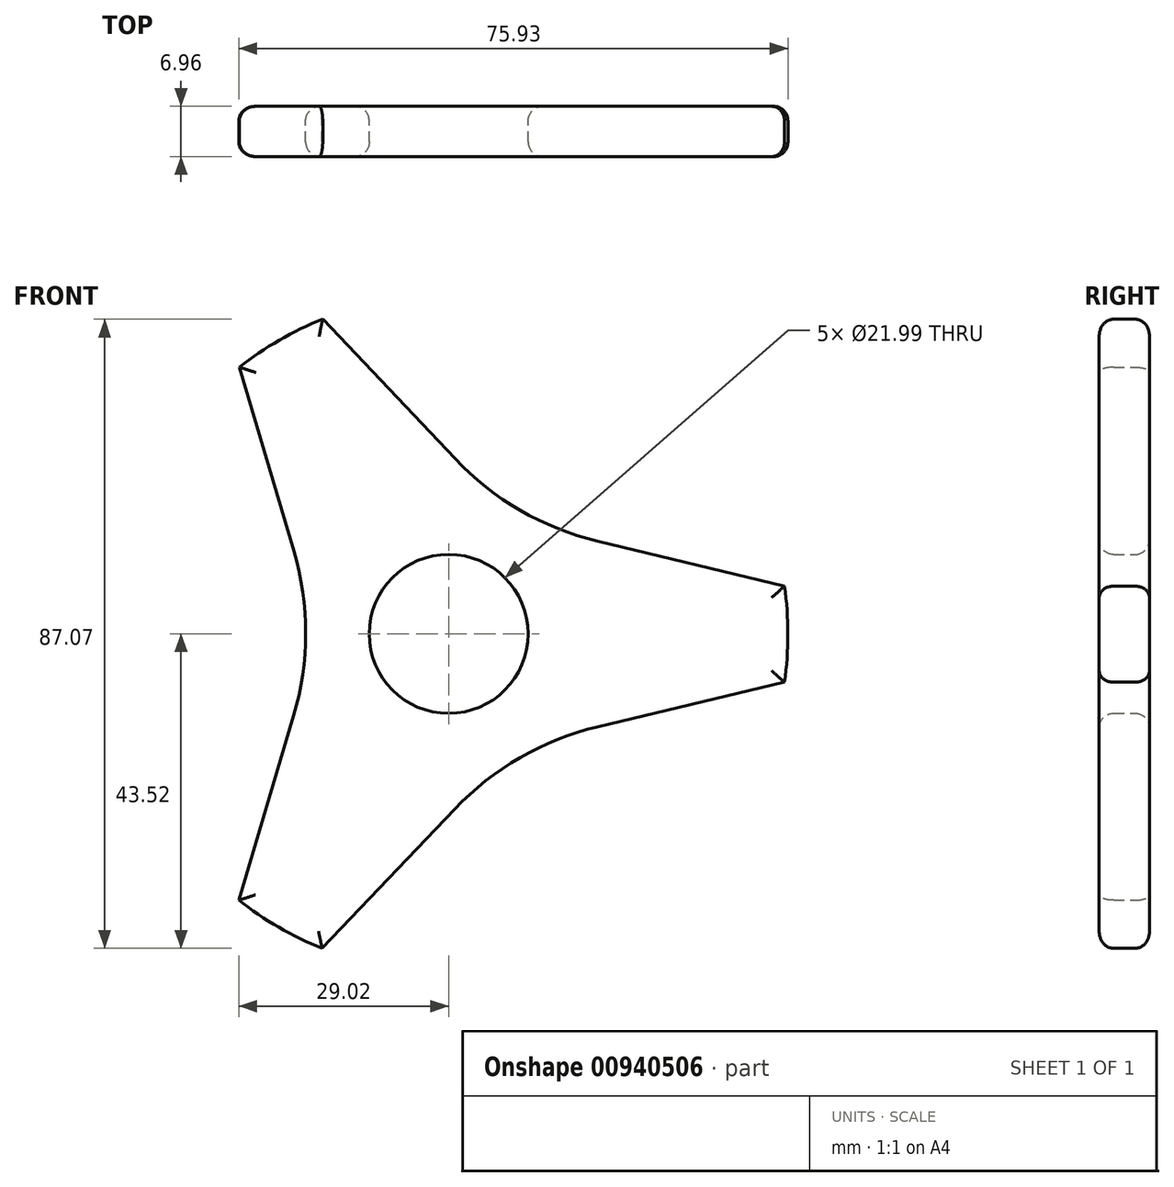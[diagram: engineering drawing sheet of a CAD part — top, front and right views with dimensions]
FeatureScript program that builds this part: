
annotation { "Feature Type Name" : "Feature", "Feature Type Description" : "" }
export const myFeature = defineFeature(function(context is Context, id is Id, definition is map)
    precondition{}
    {
        {
            var Q0;
            Q0=qCreatedBy(makeId("Front.planeOp"),FACE);
            var sketch = newSketch(context, id + "F0", { "sketchPlane" : qUnion([Q0])});
            skCircle(sketch, "E0", {"center": v(0, 0) * mm, "radius": 11 * mm});
            skCircle(sketch, "E1", {"center": v(0, 0) * mm, "radius": 17.3 * mm});
            skPoint(sketch, "E2.0.midPoint", {"position": v(55.6, -32.17) * mm});
            skLineSegment(sketch, "E3", {"start": v(23.49, 40.6) * mm, "end": v(8.66, 14.97) * mm});
            skLineSegment(sketch, "E4", {"start": v(23.42, -40.64) * mm, "end": v(8.64, -14.99) * mm});
            skLineSegment(sketch, "E5", {"start": v(9.03, 15.62) * mm, "end": v(23.49, 40.6) * mm});
            skLineSegment(sketch, "E6", {"start": v(-28.95, 36.9) * mm, "end": v(-21.41, 11.43) * mm});
            skLineSegment(sketch, "E7", {"start": v(-21.43, -11.3) * mm, "end": v(-29.02, -36.85) * mm});
            skLineSegment(sketch, "E8", {"start": v(-17.5, -43.52) * mm, "end": v(0.84, -24.23) * mm});
            skLineSegment(sketch, "E9", {"start": v(20.54, -12.88) * mm, "end": v(46.43, -6.7) * mm});
            skArc(sketch, "E10", {"start": v(46.43, -6.7) * mm, "mid": v(46.9, -0.04) * mm, "end": v(46.44, 6.61) * mm});
            skPoint(sketch, "E11.visualSharp", {"position": v(9.03, 15.62) * mm});
            skPoint(sketch, "E12.visualSharp", {"position": v(-18.05, 0.06) * mm});
            skArc(sketch, "E12.filletArc", {"start": v(-21.43, -11.3) * mm, "mid": v(-19.77, 0.06) * mm, "end": v(-21.41, 11.43) * mm});
            skArc(sketch, "E13.filletArc", {"start": v(0.88, 24.23) * mm, "mid": v(9.9, 17.1) * mm, "end": v(20.56, 12.84) * mm});
            skPoint(sketch, "E14.visualSharp", {"position": v(9, -15.63) * mm});
            skArc(sketch, "E14.filletArc", {"start": v(20.54, -12.88) * mm, "mid": v(9.87, -17.12) * mm, "end": v(0.84, -24.23) * mm});
            skLineSegment(sketch, "E15.trimOffspring", {"start": v(-17.42, 43.55) * mm, "end": v(0.88, 24.23) * mm});
            skLineSegment(sketch, "E16.trimOffspring", {"start": v(-23.42, 40.64) * mm, "end": v(-8.64, 14.99) * mm});
            skLineSegment(sketch, "E17.trimOffspring", {"start": v(-19.77, 0.02) * mm, "end": v(-17.3, 0.01) * mm});
            skPoint(sketch, "E18.start.orphan", {"position": v(-74.18, 0.06) * mm});
            skLineSegment(sketch, "E19.trimOffspring", {"start": v(-23.49, -40.6) * mm, "end": v(-8.66, -14.97) * mm});
            skPoint(sketch, "E20.orphan", {"position": v(37.03, -64.27) * mm});
            skLineSegment(sketch, "E21.trimOffspring", {"start": v(46.9, -0.04) * mm, "end": v(17.3, -0.01) * mm});
            skLineSegment(sketch, "E22", {"start": v(20.56, 12.84) * mm, "end": v(46.44, 6.61) * mm});
            skPoint(sketch, "E23.start.orphan", {"position": v(74.18, -0.06) * mm});
            skArc(sketch, "E24.trimOffspring", {"start": v(-17.42, 43.55) * mm, "mid": v(-23.42, 40.64) * mm, "end": v(-28.95, 36.9) * mm});
            skArc(sketch, "E25.trimOffspring", {"start": v(-29.02, -36.85) * mm, "mid": v(-23.5, -40.6) * mm, "end": v(-17.5, -43.52) * mm});
            skSolve(sketch);
        }
        {
            var Q0;
            Q0 = qSketchRegion(id + "F0", true);
            var Q1;
            Q1=makeQuery(id+"F0.imprint","IMPRINT",FACE,{"disambiguationData":[TD([[makeQuery(id+"F0.imprint","IMPRINT",EDGE,{"derivedFrom":sQuery(id+"F0.wireOp",EDGE,"E0")}),-1.0]])]});
            extrude(context, id + "F1", {"entities" : qUnion([Q0, Q1]), "depth" : 6.96 * mm, "offsetDistance" : 25 * mm});
        }
        {
            var Q0;
            Q0=makeQuery(id+"F1.opExtrude","CAP_FACE",FACE,{"disambiguationData":[OSD([sQuery(id+"F0.wireOp",EDGE,"E1"),sQuery(id+"F0.wireOp",EDGE,"E6"),sQuery(id+"F0.wireOp",EDGE,"E7"),sQuery(id+"F0.wireOp",EDGE,"E8"),sQuery(id+"F0.wireOp",EDGE,"E9"),sQuery(id+"F0.wireOp",EDGE,"E10"),sQuery(id+"F0.wireOp",EDGE,"E12.filletArc"),sQuery(id+"F0.wireOp",EDGE,"E13.filletArc"),sQuery(id+"F0.wireOp",EDGE,"E14.filletArc"),sQuery(id+"F0.wireOp",EDGE,"E15.trimOffspring"),sQuery(id+"F0.wireOp",EDGE,"E22"),sQuery(id+"F0.wireOp",EDGE,"E24.trimOffspring"),sQuery(id+"F0.wireOp",EDGE,"E25.trimOffspring")])],"isStart":false});
            var Q1;
            Q1=makeQuery(id+"F1.opExtrude","CAP_FACE",FACE,{"disambiguationData":[OSD([sQuery(id+"F0.wireOp",EDGE,"E1"),sQuery(id+"F0.wireOp",EDGE,"E6"),sQuery(id+"F0.wireOp",EDGE,"E7"),sQuery(id+"F0.wireOp",EDGE,"E8"),sQuery(id+"F0.wireOp",EDGE,"E9"),sQuery(id+"F0.wireOp",EDGE,"E10"),sQuery(id+"F0.wireOp",EDGE,"E12.filletArc"),sQuery(id+"F0.wireOp",EDGE,"E13.filletArc"),sQuery(id+"F0.wireOp",EDGE,"E14.filletArc"),sQuery(id+"F0.wireOp",EDGE,"E15.trimOffspring"),sQuery(id+"F0.wireOp",EDGE,"E22"),sQuery(id+"F0.wireOp",EDGE,"E24.trimOffspring"),sQuery(id+"F0.wireOp",EDGE,"E25.trimOffspring")])],"isStart":true});
            fillet(context, id + "F2", {"entities" : qUnion([Q0, Q1]), "radius" : 2 * mm, "tangentPropagation" : true, "allowEdgeOverflow" : false});
        }
    });
